# Revit family: JOMA_(4)433, (4)434 & (4)435
name_source: partatom
category: Structural Connections
revit_build: Autodesk Revit Structure 2012 (Build: 20110309_2315(x64)
units: mm (PartAtom-declared; Revit-internal decimal feet)

## types (6) — shared parameters
Länk Joma Dimensioneringsverktyg = http://www.joma.se
Material = Varmförzinkad stålplåt
zero-valued in all types: Default Elevation

## per-type parameters (varying)
| type | Typ | Vikt | Vinkelbeslag 4433 | Vinkelbeslag 4434 | Vinkelbeslag 4435 | b | h | ir | l | t | yr |
| 4340000 | VINKEL 434 | 0,43 | No | Yes | No | 80 mm  [stored 0.262467 ft] | 163 mm  [stored 0.534777 ft] | 3.843 mm | 83 mm  [stored 0.27231 ft] | 3 mm  [stored 0.00984252 ft] | 6.843 mm |
| 4330000 | VINKEL 433 | 0,314 | Yes | No | No | 60 mm  [stored 0.19685 ft] | 163 mm  [stored 0.534777 ft] | 3.843 mm | 83 mm  [stored 0.27231 ft] | 3 mm  [stored 0.00984252 ft] | 6.843 mm |
| 4350000 | VINKEL 435 | 0,314 | No | No | Yes | 100 mm  [stored 0.328084 ft] | 163 mm  [stored 0.534777 ft] | 3.843 mm | 83 mm  [stored 0.27231 ft] | 3 mm  [stored 0.00984252 ft] | 6.843 mm |
| 4433000 | VINKEL 4433 | 0,434 | Yes | No | No | 60 mm  [stored 0.19685 ft] | 164 mm  [stored 0.538058 ft] | 5.124 mm  [stored 0.016811 ft] | 83.45 mm | 4 mm  [stored 0.0131234 ft] | 9.124 mm |
| 4434000 | VINKEL 4434 | 0,572 | No | Yes | No | 80 mm  [stored 0.262467 ft] | 164 mm  [stored 0.538058 ft] | 5.124 mm  [stored 0.016811 ft] | 83.45 mm | 4 mm  [stored 0.0131234 ft] | 9.124 mm |
| 4435000 | VINKEL 4435 | 0,712 | No | No | Yes | 100 mm  [stored 0.328084 ft] | 164 mm  [stored 0.538058 ft] | 5.124 mm  [stored 0.016811 ft] | 83.45 mm | 4 mm  [stored 0.0131234 ft] | 9.124 mm |

note: [stored X ft] marks values corroborated as IEEE doubles in the binary element streams (Revit-internal decimal feet)

## geometry (parser evidence)
native form markers: Sweep x3
no freeform markers — native parametric forms only
